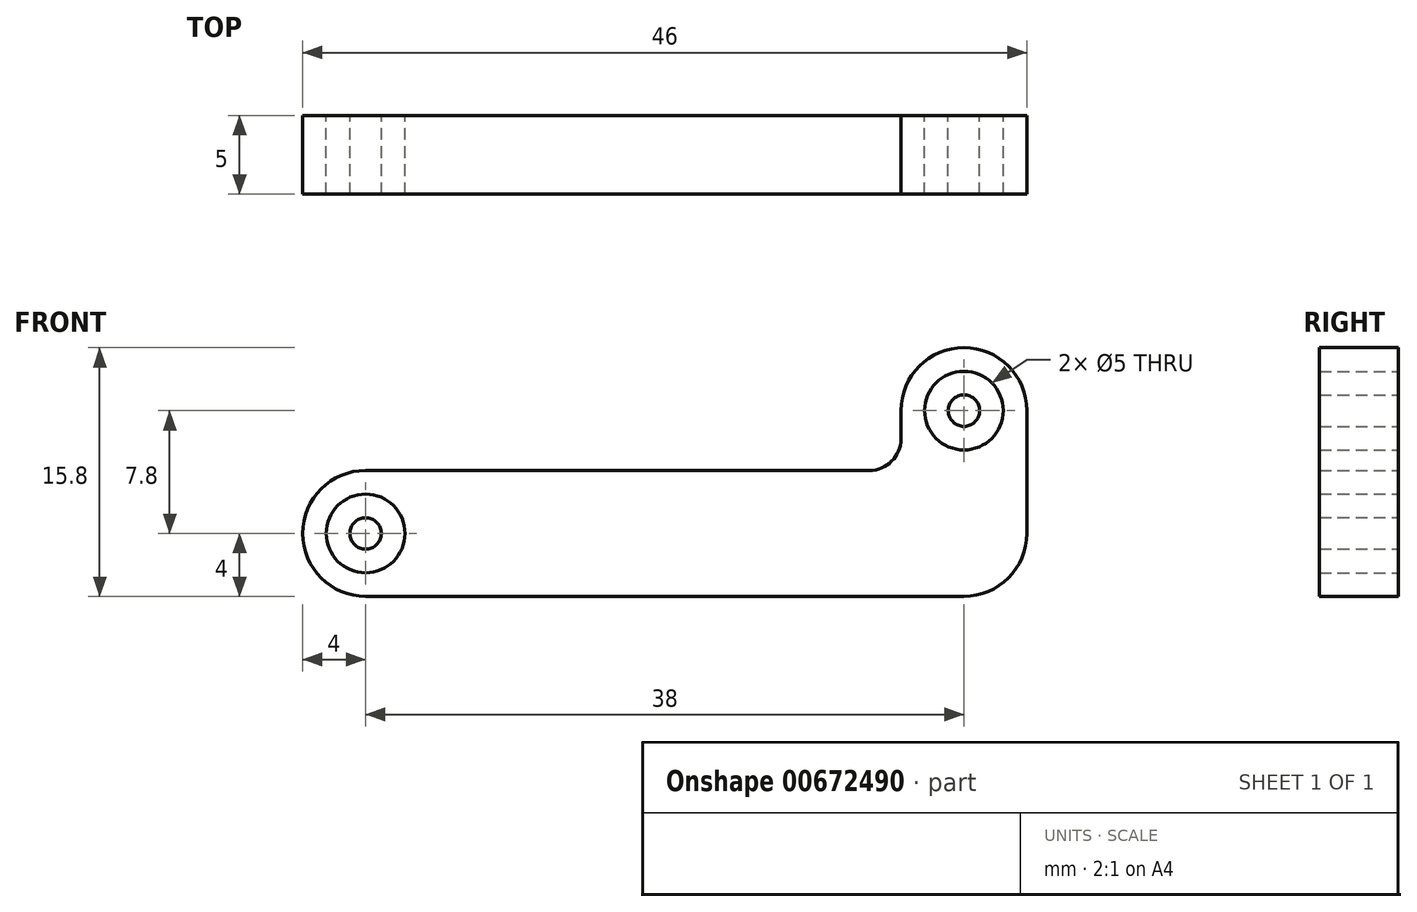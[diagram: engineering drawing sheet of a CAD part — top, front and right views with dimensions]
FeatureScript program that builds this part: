
annotation { "Feature Type Name" : "Feature", "Feature Type Description" : "" }
export const myFeature = defineFeature(function(context is Context, id is Id, definition is map)
    precondition{}
    {
        {
            var Q0;
            Q0=qCreatedBy(makeId("Front.planeOp"),FACE);
            var sketch = newSketch(context, id + "F0", { "sketchPlane" : qUnion([Q0])});
            skArc(sketch, "E0", {"start": v(0, 4) * mm, "mid": v(-4, 0) * mm, "end": v(0, -4) * mm});
            skCircle(sketch, "E1", {"center": v(0, 0) * mm, "radius": 2.5 * mm});
            skArc(sketch, "E2", {"start": v(42, 7.8) * mm, "mid": v(38, 11.8) * mm, "end": v(34, 7.8) * mm});
            skCircle(sketch, "E3", {"center": v(38, 7.8) * mm, "radius": 2.5 * mm});
            skLineSegment(sketch, "E4", {"start": v(0, 4) * mm, "end": v(32, 4) * mm});
            skLineSegment(sketch, "E5", {"start": v(34, 7.8) * mm, "end": v(34, 6) * mm});
            skLineSegment(sketch, "E6", {"start": v(0, -4) * mm, "end": v(38, -4) * mm});
            skLineSegment(sketch, "E7", {"start": v(42, 7.8) * mm, "end": v(42, 0) * mm});
            skPoint(sketch, "E8.visualSharp", {"position": v(34, 4) * mm});
            skArc(sketch, "E8.filletArc", {"start": v(32, 4) * mm, "mid": v(33.41, 4.59) * mm, "end": v(34, 6) * mm});
            skPoint(sketch, "E9.visualSharp", {"position": v(42, -4) * mm});
            skArc(sketch, "E9.filletArc", {"start": v(38, -4) * mm, "mid": v(40.83, -2.83) * mm, "end": v(42, 0) * mm});
            skCircle(sketch, "E10", {"center": v(0, 0) * mm, "radius": 1 * mm});
            skCircle(sketch, "E11", {"center": v(38, 7.8) * mm, "radius": 1 * mm});
            skSolve(sketch);
        }
        {
            var Q0;
            Q0=makeQuery(id+"F0.imprint","IMPRINT",FACE,{"disambiguationData":[TD([[makeQuery(id+"F0.imprint","IMPRINT",EDGE,{"derivedFrom":sQuery(id+"F0.wireOp",EDGE,"E0")}),1.0]])]});
            var Q1;
            Q1=makeQuery(id+"F0.imprint","IMPRINT",FACE,{"disambiguationData":[TD([[makeQuery(id+"F0.imprint","IMPRINT",EDGE,{"derivedFrom":sQuery(id+"F0.wireOp",EDGE,"E10")}),1.0]])]});
            var Q2;
            Q2=makeQuery(id+"F0.imprint","IMPRINT",FACE,{"disambiguationData":[TD([[makeQuery(id+"F0.imprint","IMPRINT",EDGE,{"derivedFrom":sQuery(id+"F0.wireOp",EDGE,"E11")}),1.0]])]});
            extrude(context, id + "F1", {"entities" : qUnion([Q0, Q1, Q2]), "endBound" : BoundingType.SYMMETRIC, "depth" : 5 * mm, "offsetDistance" : 25 * mm});
        }
    });
